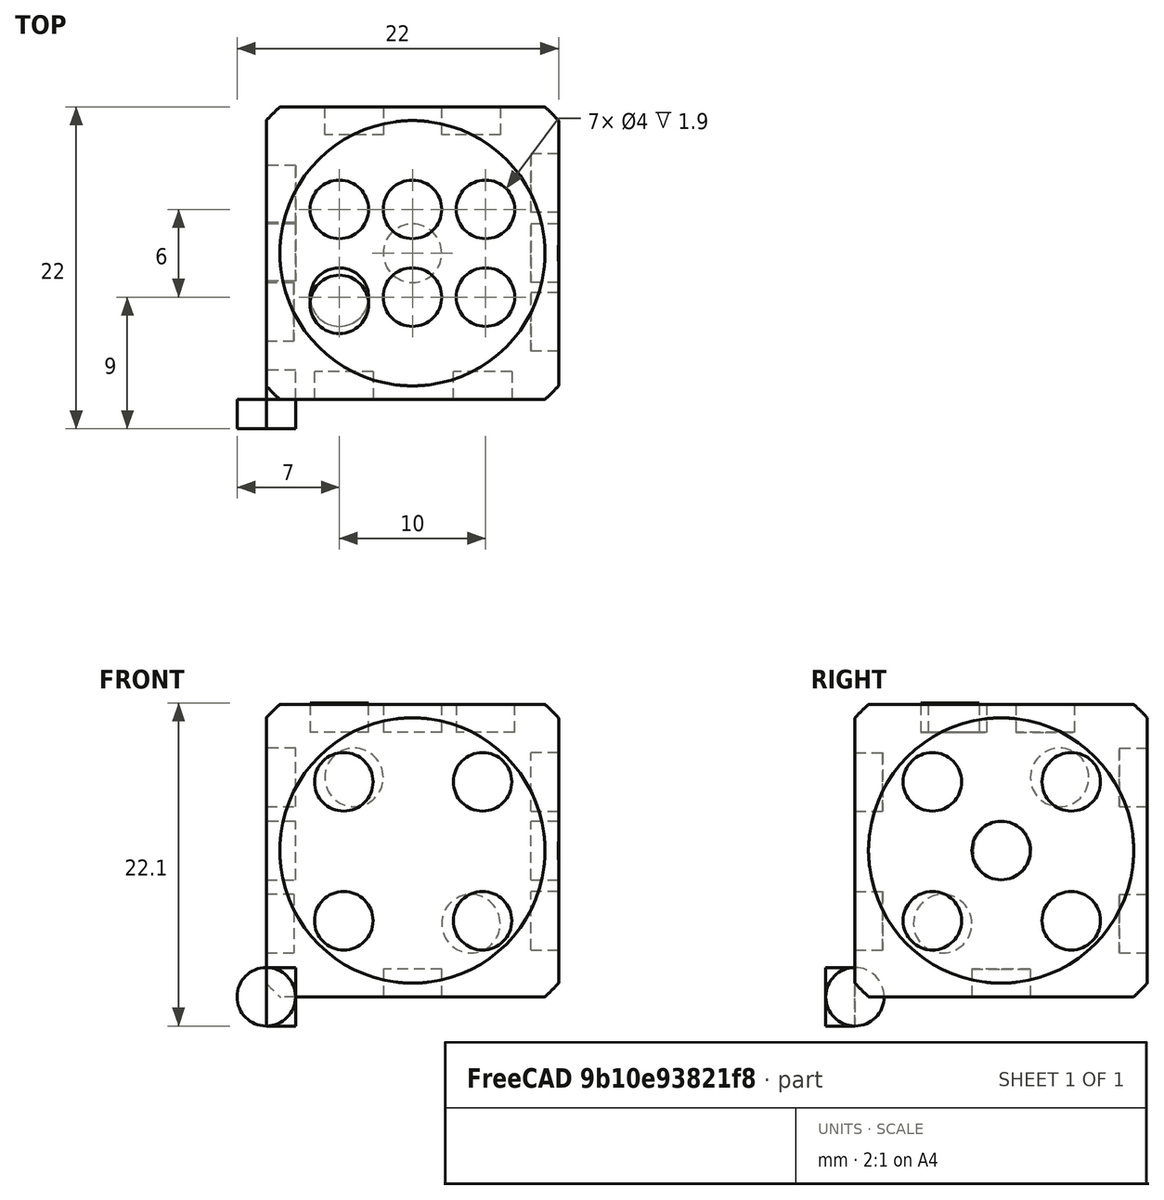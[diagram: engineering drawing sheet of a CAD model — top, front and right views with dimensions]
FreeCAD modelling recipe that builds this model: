
FCSTD DOCUMENT  (FreeCAD 0.21R33694 (Git))
Label: npatris_exercici2
License: All rights reserved
LicenseURL: https://en.wikipedia.org/wiki/All_rights_reserved
objects: Part::Cylinder×10, Part::Cut×10, Part::FeaturePython×3, Part::Box×1, Part::Fillet×1, Part::Sphere×1, Part::MultiCommon×1
note: 24 computed .brp shape members not serialized (recipe doc carries the construction recipe); baked Part::Feature solids carry a one-line shape summary decoded from their .brp

FEATURE [Part::Box] Box  label="Cub"
  AttacherType = Attacher::AttachEngine3D
  Height = 20
  Length = 20
  Width = 20
FEATURE [Part::Fillet] Fillet
  Base = -> Box
  Edges = 12 edges r=1: [Edge1,Edge2,Edge3,Edge4,Edge5,Edge6,Edge7,Edge8,Edge9,Edge10,Edge11,Edge12]
FEATURE [Part::Sphere] Sphere  label="Esfera"
  Angle1 = -90
  Angle2 = 90
  Angle3 = 360
  AttacherType = Attacher::AttachEngine3D
  Placement = pos=(10,10,10) rot=(0,0,1;0rad)
  Radius = 13.5
FEATURE [Part::MultiCommon] Common
  Shapes = -> [Fillet,Sphere]
FEATURE [Part::Cylinder] Cylinder  label="Cilindre"
  Angle = 360
  AttacherType = Attacher::AttachEngine3D
  FirstAngle = 0
  Height = 2
  Placement = pos=(5,6.5,18.1) rot=(0,0,1;0rad)
  Radius = 2
  SecondAngle = 0
FEATURE [Part::FeaturePython] Array  # Draft array (typed FeaturePython)
  AlwaysSyncPlacement = false
  Angle = 360
  ArrayType = 0
  Axis = (0,0,1)
  Base = -> Cylinder
  Center = (0,0,0)
  Count = 6
  ExpandArray = false
  Fuse = false
  IntervalAxis = (0,0,0)
  IntervalX = (5,0,0)
  IntervalY = (0,6,0)
  IntervalZ = (0,0,100)
  NumberCircles = 3
  NumberPolar = 5
  NumberX = 3
  NumberY = 2
  NumberZ = 1
  Placement = pos=(0,0.5,0) rot=(0,0,1;0rad)
  PlacementList = 6 placements: [(5,6.5,18.1),(5,12.5,18.1),(10,6.5,18.1),(10,12.5,18.1),(15,6.5,18.1),(15,12.5,18.1)]
  RadialDistance = 50
  ScaleList = (6) [(1,1,1),(1,1,1),(1,1,1),(1,1,1),(1,1,1),(1,1,1)]
  Symmetry = 1
  TangentialDistance = 25
FEATURE [Part::Cut] Cut
  Base = -> Common
  Tool = -> Array
FEATURE [Part::Cylinder] Cylinder001  label="Cilindre001"
  Angle = 360
  AttacherType = Attacher::AttachEngine3D
  FirstAngle = 0
  Height = 2
  Placement = pos=(1.9,6,5) rot=(0,-1,0;1.5708rad)
  Radius = 2
  SecondAngle = 0
FEATURE [Part::Cut] Cut001
  Base = -> Cut
  Tool = -> Cylinder001
FEATURE [Part::Cylinder] Cylinder002  label="Cilindre002"
  Angle = 360
  AttacherType = Attacher::AttachEngine3D
  FirstAngle = 0
  Height = 2
  Placement = pos=(0,10.1,10) rot=(0,1,0;1.5708rad)
  Radius = 2
  SecondAngle = 0
FEATURE [Part::Cut] Cut002
  Base = -> Cut001
  Tool = -> Cylinder002
FEATURE [Part::Cylinder] Cylinder003  label="Cilindre003"
  Angle = 360
  AttacherType = Attacher::AttachEngine3D
  FirstAngle = 0
  Height = 2
  Placement = pos=(0,14,15) rot=(0,1,0;1.5708rad)
  Radius = 2
  SecondAngle = 0
FEATURE [Part::Cut] Cut003
  Base = -> Cut002
  Tool = -> Cylinder003
FEATURE [Part::Cylinder] Cylinder005  label="Cilindre005"
  Angle = 360
  AttacherType = Attacher::AttachEngine3D
  FirstAngle = 0
  Height = 2
  Placement = pos=(0,0,0) rot=(1,0,0;1.5708rad)
  Radius = 2
  SecondAngle = 0
FEATURE [Part::FeaturePython] Array001  # Draft array (typed FeaturePython)
  AlwaysSyncPlacement = false
  Angle = 360
  ArrayType = 0
  Axis = (0,0,1)
  Base = -> Cylinder005
  Center = (0,0,0)
  Count = 4
  ExpandArray = false
  Fuse = false
  IntervalAxis = (0,0,0)
  IntervalX = (9.5,0,0)
  IntervalY = (0,100,0)
  IntervalZ = (0,0,9.5)
  NumberCircles = 3
  NumberPolar = 5
  NumberX = 2
  NumberY = 1
  NumberZ = 2
  Placement = pos=(5.3,1.9,5.2) rot=(0,0,1;0rad)
  PlacementList = 4 placements: [(0,0,0),(0,0,9.5),(9.5,0,0),(9.5,0,9.5)]
  RadialDistance = 50
  ScaleList = (4) [(1,1,1),(1,1,1),(1,1,1),(1,1,1)]
  Symmetry = 1
  TangentialDistance = 25
FEATURE [Part::Cut] Cut004
  Base = -> Cut003
  Tool = -> Array001
FEATURE [Part::Cylinder] Cylinder006  label="Cilindre006"
  Angle = 360
  AttacherType = Attacher::AttachEngine3D
  FirstAngle = 0
  Height = 2
  Placement = pos=(0,0,0) rot=(0,1,0;1.5708rad)
  Radius = 2
  SecondAngle = 0
FEATURE [Part::FeaturePython] Array002  # Draft array (typed FeaturePython)
  AlwaysSyncPlacement = false
  Angle = 360
  ArrayType = 0
  Axis = (0,0,1)
  Base = -> Cylinder006
  Center = (0,0,0)
  Count = 4
  ExpandArray = false
  Fuse = false
  IntervalAxis = (0,0,0)
  IntervalX = (100,0,0)
  IntervalY = (0,9.5,0)
  IntervalZ = (0,0,9.5)
  NumberCircles = 3
  NumberPolar = 5
  NumberX = 1
  NumberY = 2
  NumberZ = 2
  Placement = pos=(18.1,5.3,5.2) rot=(0,0,1;0rad)
  PlacementList = 4 placements: [(0,0,0),(0,0,9.5),(0,9.5,0),(0,9.5,9.5)]
  RadialDistance = 50
  ScaleList = (4) [(1,1,1),(1,1,1),(1,1,1),(1,1,1)]
  Symmetry = 1
  TangentialDistance = 25
FEATURE [Part::Cut] Cut005
  Base = -> Cut004
  Tool = -> Array002
FEATURE [Part::Cylinder] Cylinder007  label="Cilindre007"
  Angle = 360
  AttacherType = Attacher::AttachEngine3D
  FirstAngle = 0
  Height = 2
  Placement = pos=(18.1,10,10) rot=(0,1,0;1.5708rad)
  Radius = 2
  SecondAngle = 0
FEATURE [Part::Cut] Cut006
  Base = -> Cut005
  Tool = -> Cylinder007
FEATURE [Part::Cylinder] Cylinder008  label="Cilindre008"
  Angle = 360
  AttacherType = Attacher::AttachEngine3D
  FirstAngle = 0
  Height = 2
  Placement = pos=(10,10,-0.1) rot=(0,0,1;0rad)
  Radius = 2
  SecondAngle = 0
FEATURE [Part::Cut] Cut007
  Base = -> Cut006
  Tool = -> Cylinder008
FEATURE [Part::Cylinder] Cylinder009  label="Cilindre009"
  Angle = 360
  AttacherType = Attacher::AttachEngine3D
  FirstAngle = 0
  Height = 2
  Placement = pos=(6,20.1,15) rot=(1,0,0;1.5708rad)
  Radius = 2
  SecondAngle = 0
FEATURE [Part::Cut] Cut008
  Base = -> Cut007
  Tool = -> Cylinder009
FEATURE [Part::Cylinder] Cylinder010  label="Cilindre010"
  Angle = 360
  AttacherType = Attacher::AttachEngine3D
  FirstAngle = 0
  Height = 2
  Placement = pos=(14,20.1,5) rot=(1,0,0;1.5708rad)
  Radius = 2
  SecondAngle = 0
FEATURE [Part::Cut] Cut009
  Base = -> Cut008
  Tool = -> Cylinder010
